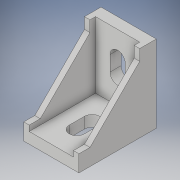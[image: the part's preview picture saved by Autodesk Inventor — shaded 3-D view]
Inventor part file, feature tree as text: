
AUTODESK INVENTOR PART (.ipt)
format: ipt  version: 2019 (Build 230136000, 136)  size: 166,912 bytes
history: native  units: in
note: dims shown in document units (in); Inventor stores cm internally (conversion verified against a paired STEP export)
features: extrude x6, sketch x6
ambient origin geometry x8: Origin, YZ Plane, XZ Plane, XY Plane, X Axis, Y Axis, Z Axis, Center Point
bodies: Solid1 (feature_tree)
feature tree (12):
  extrude  "Extrusion1"  Depth=0.7874in
  extrude  "Extrusion2"  Depth=0.1575in
  extrude  "Extrusion3"  Depth=0.0787in
  extrude  "Extrusion4"  Depth=0.9449in TaperAngle=0.0deg
  extrude  "Extrusion5"  Depth=0.0787in
  extrude  "Extrusion6"  Depth=0.1575in
  sketch  "Sketch1"  dims[d0=1.1024in d1=0.7874in]
  sketch  "Sketch2"  dims[d2=0.1575in d3=0.0in d4=0.1575in]
  sketch  "Sketch3"  dims[d5=0.9449in d6=0.0in d7=0.0787in]
  sketch  "Sketch4"  dims[d8=0.0787in d9=0.9449in d10=0.0in]
  sketch  "Sketch5"  dims[d11=0.0787in d12=0.0787in]
  sketch  "Sketch6"  dims[d13=0.1575in d14=0.1575in d15=0.9449in d16=0.0in d17=0.2165in d18=0.2165in d19=0.9449in d20=0.0in d21=0.2165in d22=0.2165in d23=0.9449in d24=0.0in]
